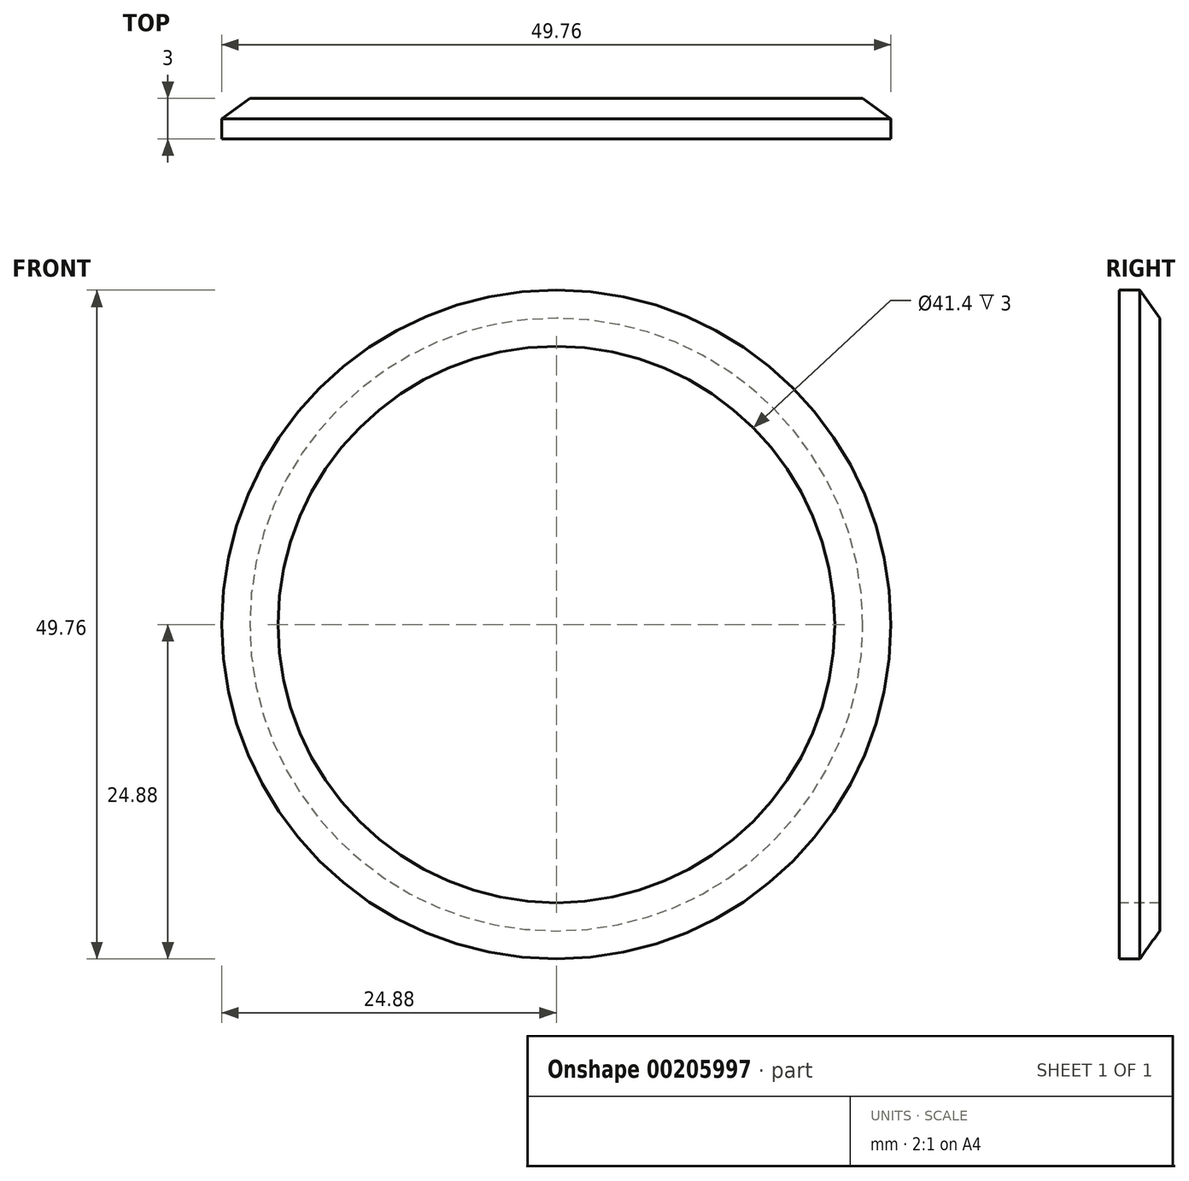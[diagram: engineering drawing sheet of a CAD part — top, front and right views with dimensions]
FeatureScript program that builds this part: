
annotation { "Feature Type Name" : "Feature", "Feature Type Description" : "" }
export const myFeature = defineFeature(function(context is Context, id is Id, definition is map)
    precondition{}
    {
        {
            var Q0;
            Q0=qCreatedBy(makeId("Right.planeOp"),FACE);
            var sketch = newSketch(context, id + "F0", { "sketchPlane" : qUnion([Q0])});
            skLineSegment(sketch, "E0.bottom", {"start": v(0, 24.88) * mm, "end": v(1.5, 24.88) * mm});
            skLineSegment(sketch, "E0.top", {"start": v(0, 20.7) * mm, "end": v(3, 20.7) * mm});
            skLineSegment(sketch, "E0.left", {"start": v(0, 24.88) * mm, "end": v(0, 20.7) * mm});
            skLineSegment(sketch, "E0.right", {"start": v(3, 22.79) * mm, "end": v(3, 20.7) * mm});
            skLineSegment(sketch, "E1", {"start": v(1.5, 24.88) * mm, "end": v(3, 22.79) * mm});
            skPoint(sketch, "E2.orphan", {"position": v(3, 24.88) * mm});
            skSolve(sketch);
        }
        {
            var Q0;
            Q0=qCreatedBy(makeId("Right.planeOp"),FACE);
            var sketch = newSketch(context, id + "F1", { "sketchPlane" : qUnion([Q0])});
            skLineSegment(sketch, "E3", {"start": v(0, 0) * mm, "end": v(15.77, 0) * mm});
            skSolve(sketch);
        }
        {
            var Q0;
            Q0=makeQuery(id+"F0.imprint","IMPRINT",FACE,{"disambiguationData":[TD([[makeQuery(id+"F0.imprint","IMPRINT",EDGE,{"derivedFrom":sQuery(id+"F0.wireOp",EDGE,"E0.bottom")}),-1.0]])]});
            var Q1;
            Q1=sQuery(id+"F1.wireOp",EDGE,"E3");
            revolve(context, id + "F2", {"entities" : qUnion([Q0]), "axis" : qUnion([Q1]), "revolveType" : RevolveType.FULL});
        }
    });
